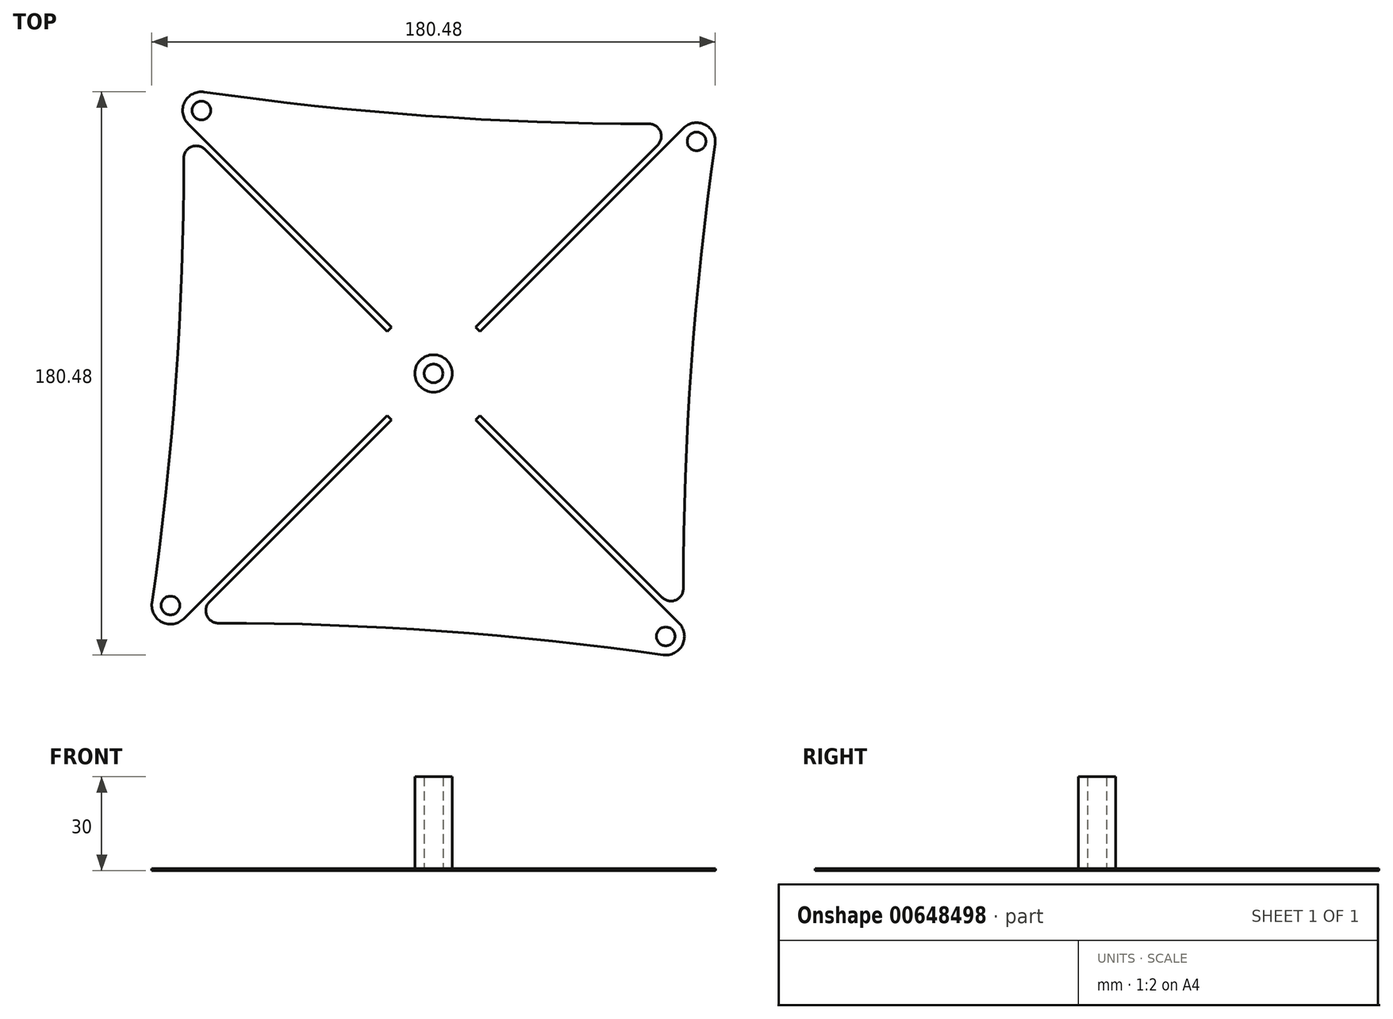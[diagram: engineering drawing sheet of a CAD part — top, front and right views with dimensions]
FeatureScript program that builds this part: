
annotation { "Feature Type Name" : "Feature", "Feature Type Description" : "" }
export const myFeature = defineFeature(function(context is Context, id is Id, definition is map)
    precondition{}
    {
        {
            var Q0;
            Q0=qCreatedBy(makeId("Top.planeOp"),FACE);
            var sketch = newSketch(context, id + "F0", { "sketchPlane" : qUnion([Q0])});
            skLineSegment(sketch, "E0.bottom", {"start": v(68.85, 80) * mm, "end": v(68.93, 80) * mm});
            skLineSegment(sketch, "E0.top", {"start": v(-68.93, -80) * mm, "end": v(-68.85, -80) * mm});
            skLineSegment(sketch, "E0.left", {"start": v(-80, 68.93) * mm, "end": v(-80, 68.85) * mm});
            skLineSegment(sketch, "E0.right", {"start": v(80, -68.85) * mm, "end": v(80, -68.93) * mm});
            skLineSegment(sketch, "E1", {"start": v(-14.14, 14.14) * mm, "end": v(0, 0) * mm, "construction": true});
            skLineSegment(sketch, "E2", {"start": v(0, 0) * mm, "end": v(14.14, 14.14) * mm, "construction": true});
            skLineSegment(sketch, "E3", {"start": v(0, 0) * mm, "end": v(10.35, -38.64) * mm, "construction": true});
            skLineSegment(sketch, "E4", {"start": v(0, 0) * mm, "end": v(14.14, -14.14) * mm, "construction": true});
            skLineSegment(sketch, "E5", {"start": v(-73.17, 71.76) * mm, "end": v(-14.85, 13.44) * mm});
            skLineSegment(sketch, "E6", {"start": v(-14.85, 13.44) * mm, "end": v(-13.44, 14.85) * mm});
            skLineSegment(sketch, "E7", {"start": v(-13.44, 14.85) * mm, "end": v(-78.59, 80) * mm});
            skLineSegment(sketch, "E8.MirrorCS", {"start": v(80, 78.59) * mm, "end": v(14.85, 13.44) * mm});
            skLineSegment(sketch, "E9.MirrorCS", {"start": v(13.44, 14.85) * mm, "end": v(71.76, 73.17) * mm});
            skLineSegment(sketch, "E10.MirrorCS", {"start": v(14.85, 13.44) * mm, "end": v(13.44, 14.85) * mm});
            skLineSegment(sketch, "E11.MirrorCS", {"start": v(73.17, -71.76) * mm, "end": v(14.85, -13.44) * mm});
            skLineSegment(sketch, "E12.MirrorCS", {"start": v(13.44, -14.85) * mm, "end": v(78.59, -80) * mm});
            skLineSegment(sketch, "E13.MirrorCS", {"start": v(14.85, -13.44) * mm, "end": v(13.44, -14.85) * mm});
            skLineSegment(sketch, "E14.MirrorCS", {"start": v(-14.85, -13.44) * mm, "end": v(-13.44, -14.85) * mm});
            skLineSegment(sketch, "E15.MirrorCS", {"start": v(-13.44, -14.85) * mm, "end": v(-71.76, -73.17) * mm});
            skLineSegment(sketch, "E16.MirrorCS", {"start": v(-80, -78.59) * mm, "end": v(-14.85, -13.44) * mm});
            skPoint(sketch, "E17.orphan", {"position": v(-82.73, -81.32) * mm});
            skPoint(sketch, "E18.orphan", {"position": v(-81.32, -82.73) * mm});
            skPoint(sketch, "E19.orphan", {"position": v(81.32, -82.73) * mm});
            skPoint(sketch, "E20.orphan", {"position": v(80, -80) * mm});
            skPoint(sketch, "E21.orphan", {"position": v(82.73, -81.32) * mm});
            skPoint(sketch, "E22.orphan", {"position": v(82.73, 81.32) * mm});
            skPoint(sketch, "E23.orphan", {"position": v(81.32, 82.73) * mm});
            skPoint(sketch, "E24.orphan", {"position": v(80, 80) * mm});
            skPoint(sketch, "E25.start.orphan", {"position": v(-81.32, 82.73) * mm});
            skPoint(sketch, "E26.orphan", {"position": v(-82.73, 81.32) * mm});
            skPoint(sketch, "E27.orphan", {"position": v(-80, 80) * mm});
            skCircle(sketch, "E28", {"center": v(0, 0) * mm, "radius": 3 * mm});
            skArc(sketch, "E29", {"start": v(-73.49, 90.18) * mm, "mid": v(-79.7, 86.93) * mm, "end": v(-78.59, 80) * mm});
            skCircle(sketch, "E30", {"center": v(-74.34, 84.24) * mm, "radius": 3 * mm});
            skArc(sketch, "E31", {"start": v(90.18, 73.49) * mm, "mid": v(86.93, 79.7) * mm, "end": v(80, 78.59) * mm});
            skCircle(sketch, "E32", {"center": v(84.24, 74.34) * mm, "radius": 3 * mm});
            skArc(sketch, "E33", {"start": v(73.49, -90.18) * mm, "mid": v(79.7, -86.93) * mm, "end": v(78.59, -80) * mm});
            skCircle(sketch, "E34", {"center": v(74.34, -84.24) * mm, "radius": 3 * mm});
            skArc(sketch, "E35", {"start": v(-90.18, -73.49) * mm, "mid": v(-86.93, -79.7) * mm, "end": v(-80, -78.59) * mm});
            skCircle(sketch, "E36", {"center": v(-84.24, -74.34) * mm, "radius": 3 * mm});
            skPoint(sketch, "E37.visualSharp", {"position": v(80, 70.1) * mm});
            skArc(sketch, "E37.filletArc", {"start": v(90.18, 73.49) * mm, "mid": v(82.55, 2.5) * mm, "end": v(80, -68.85) * mm});
            skPoint(sketch, "E38.visualSharp", {"position": v(-70.1, 80) * mm});
            skArc(sketch, "E38.filletArc", {"start": v(-73.49, 90.18) * mm, "mid": v(-2.5, 82.55) * mm, "end": v(68.85, 80) * mm});
            skPoint(sketch, "E39.visualSharp", {"position": v(-80, -70.1) * mm});
            skArc(sketch, "E39.filletArc", {"start": v(-90.18, -73.49) * mm, "mid": v(-82.55, -2.5) * mm, "end": v(-80, 68.85) * mm});
            skPoint(sketch, "E40.visualSharp", {"position": v(70.1, -80) * mm});
            skArc(sketch, "E40.filletArc", {"start": v(73.49, -90.18) * mm, "mid": v(2.5, -82.55) * mm, "end": v(-68.85, -80) * mm});
            skPoint(sketch, "E41.visualSharp", {"position": v(78.59, 80) * mm});
            skArc(sketch, "E41.filletArc", {"start": v(71.76, 73.17) * mm, "mid": v(72.62, 77.53) * mm, "end": v(68.93, 80) * mm});
            skPoint(sketch, "E42.visualSharp", {"position": v(80, -78.59) * mm});
            skArc(sketch, "E42.filletArc", {"start": v(73.17, -71.76) * mm, "mid": v(77.53, -72.62) * mm, "end": v(80, -68.93) * mm});
            skPoint(sketch, "E43.visualSharp", {"position": v(-78.59, -80) * mm});
            skArc(sketch, "E43.filletArc", {"start": v(-71.76, -73.17) * mm, "mid": v(-72.62, -77.53) * mm, "end": v(-68.93, -80) * mm});
            skPoint(sketch, "E44.visualSharp", {"position": v(-80, 78.59) * mm});
            skArc(sketch, "E44.filletArc", {"start": v(-73.17, 71.76) * mm, "mid": v(-77.53, 72.62) * mm, "end": v(-80, 68.93) * mm});
            skSolve(sketch);
        }
        {
            var Q0;
            Q0=qCreatedBy(makeId("Top.planeOp"),FACE);
            var sketch = newSketch(context, id + "F1", { "sketchPlane" : qUnion([Q0])});
            skCircle(sketch, "E45", {"center": v(0, 0) * mm, "radius": 6 * mm});
            skCircle(sketch, "E46.0", {"center": v(0, 0) * mm, "radius": 3 * mm});
            skSolve(sketch);
        }
        {
            var Q0;
            Q0 = qSketchRegion(id + "F1", true);
            extrude(context, id + "F2", {"entities" : qUnion([Q0]), "depth" : 30 * mm, "offsetDistance" : 25 * mm});
        }
        {
            var Q0;
            Q0=makeQuery(id+"F0.imprint","IMPRINT",FACE,{"disambiguationData":[TD([[makeQuery(id+"F0.imprint","IMPRINT",EDGE,{"derivedFrom":sQuery(id+"F0.wireOp",EDGE,"E0.bottom")}),-1.0]])]});
            extrude(context, id + "F3", {"entities" : qUnion([Q0]), "operationType" : NewBodyOperationType.ADD, "depth" : 0.64 * mm, "offsetDistance" : 25 * mm});
        }
    });
